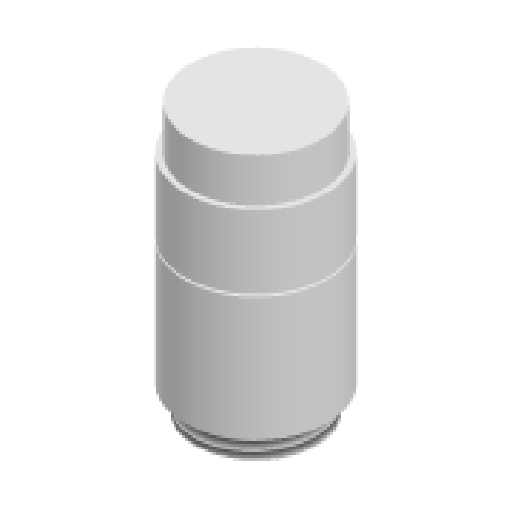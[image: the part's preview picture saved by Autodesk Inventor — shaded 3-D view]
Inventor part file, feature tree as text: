
AUTODESK INVENTOR PART (.ipt)
format: ipt  version: 2024.1 (Build 281209000, 209)  size: 124,416 bytes
history: native  units: mm
features: revolve x1, thread x1, sketch x1
ambient origin geometry x8: Origin, YZ Plane, XZ Plane, XY Plane, X Axis, Y Axis, Z Axis, Center Point
bodies: Volumenkörper1 (feature_tree)
feature tree (3):
  revolve  "Umdrehung1"
  thread  "Gewinde1"  [1 undecoded]
  sketch  "Skizze1"  dims[d1=9.0mm d2=90.0deg d3=1.1mm d4=270.0deg d5=0.5mm d6=1.0mm d7=15.0mm d8=360.0deg d9=13.95mm d10=2.7mm d11=5.0mm d12=0.0mm d13=12.5mm d14=5.0mm]
note: 1 required parameter value undecoded (feature->parameter linkage not recoverable at this tier; creation-order binding heuristic only, values carry confidence <= 0.55)
